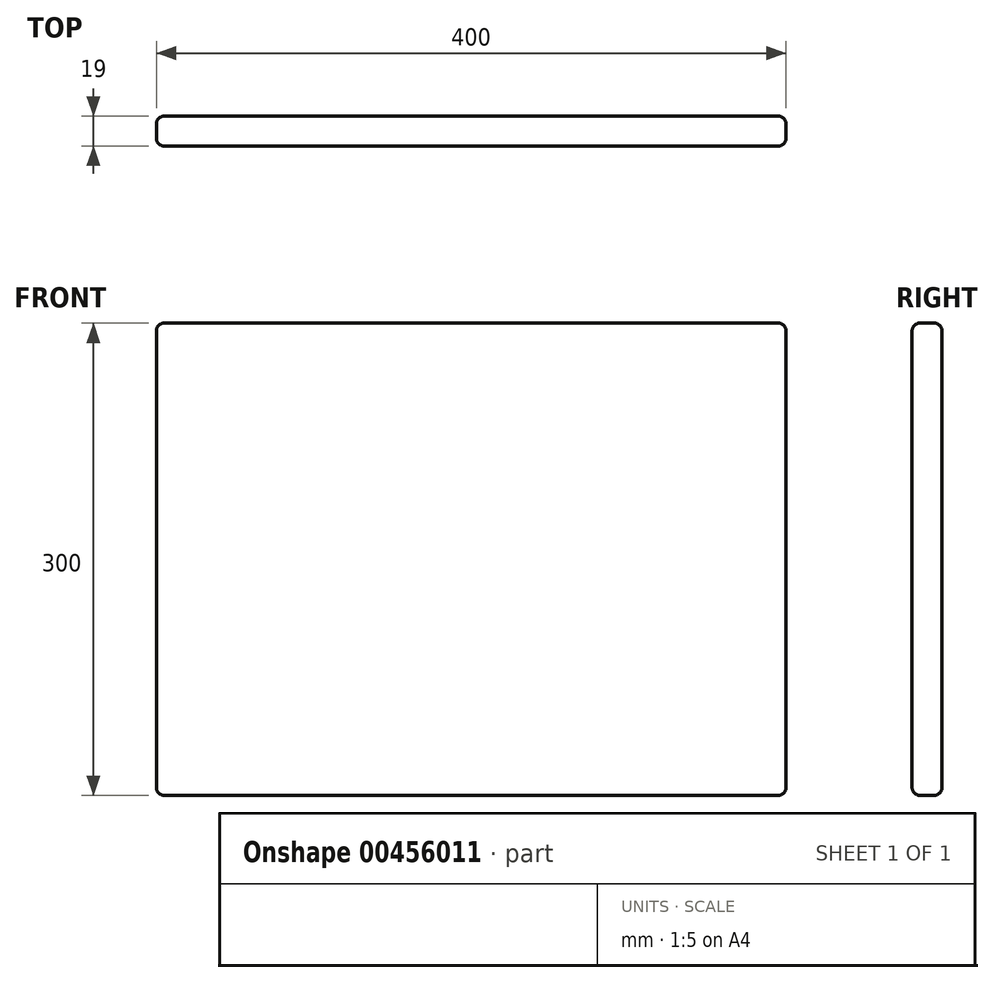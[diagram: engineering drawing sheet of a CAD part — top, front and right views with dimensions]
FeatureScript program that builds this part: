
annotation { "Feature Type Name" : "Feature", "Feature Type Description" : "" }
export const myFeature = defineFeature(function(context is Context, id is Id, definition is map)
    precondition{}
    {
        {
            var Q0;
            Q0=qCreatedBy(makeId("Front.planeOp"),FACE);
            var sketch = newSketch(context, id + "F0", { "sketchPlane" : qUnion([Q0])});
            skLineSegment(sketch, "E0", {"start": v(0, 0) * mm, "end": v(400, 0) * mm});
            skLineSegment(sketch, "E1", {"start": v(400, 0) * mm, "end": v(400, 300) * mm});
            skLineSegment(sketch, "E2", {"start": v(400, 300) * mm, "end": v(0, 300) * mm});
            skLineSegment(sketch, "E3", {"start": v(0, 300) * mm, "end": v(0, 0) * mm});
            skSolve(sketch);
        }
        {
            var Q0;
            Q0=makeQuery(id+"F0.imprint","IMPRINT",FACE,{"disambiguationData":[TD([[makeQuery(id+"F0.imprint","IMPRINT",EDGE,{"derivedFrom":sQuery(id+"F0.wireOp",EDGE,"E0")}),1.0]])]});
            extrude(context, id + "F1", {"entities" : qUnion([Q0]), "depth" : 19 * mm});
        }
        {
            var Q0;
            Q0=makeQuery(id+"F1.opExtrude","CAP_FACE",FACE,{"disambiguationData":[OSD([sQuery(id+"F0.wireOp",EDGE,"E0"),sQuery(id+"F0.wireOp",EDGE,"E1"),sQuery(id+"F0.wireOp",EDGE,"E2"),sQuery(id+"F0.wireOp",EDGE,"E3")])],"isStart":false});
            var Q1;
            Q1=makeQuery(id+"F1.opExtrude","SWEPT_FACE",FACE,{"disambiguationData":[OSD([sQuery(id+"F0.wireOp",EDGE,"E0")])]});
            var Q2;
            Q2=makeQuery(id+"F1.opExtrude","SWEPT_EDGE",EDGE,{"disambiguationData":[OSD([sQuery(id+"F0.wireOp",EDGE,"E0"),sQuery(id+"F0.wireOp",EDGE,"E1")])]});
            var Q3;
            Q3=makeQuery(id+"F1.opExtrude","SWEPT_EDGE",EDGE,{"disambiguationData":[OSD([sQuery(id+"F0.wireOp",EDGE,"E2"),sQuery(id+"F0.wireOp",EDGE,"E3")])]});
            var Q4;
            Q4=makeQuery(id+"F1.opExtrude","SWEPT_FACE",FACE,{"disambiguationData":[OSD([sQuery(id+"F0.wireOp",EDGE,"E1")])]});
            var Q5;
            Q5=makeQuery(id+"F1.opExtrude","SWEPT_FACE",FACE,{"disambiguationData":[OSD([sQuery(id+"F0.wireOp",EDGE,"E2")])]});
            var Q6;
            Q6=makeQuery(id+"F1.opExtrude","SWEPT_FACE",FACE,{"disambiguationData":[OSD([sQuery(id+"F0.wireOp",EDGE,"E3")])]});
            var Q7;
            Q7=makeQuery(id+"F1.opExtrude","CAP_EDGE",EDGE,{"disambiguationData":[OSD([sQuery(id+"F0.wireOp",EDGE,"E1")])],"isStart":false});
            var Q8;
            Q8=makeQuery(id+"F1.opExtrude","CAP_EDGE",EDGE,{"disambiguationData":[OSD([sQuery(id+"F0.wireOp",EDGE,"E2")])],"isStart":false});
            var Q9;
            Q9=makeQuery(id+"F1.opExtrude","CAP_EDGE",EDGE,{"disambiguationData":[OSD([sQuery(id+"F0.wireOp",EDGE,"E3")])],"isStart":true});
            var Q10;
            Q10=makeQuery(id+"F1.opExtrude","CAP_EDGE",EDGE,{"disambiguationData":[OSD([sQuery(id+"F0.wireOp",EDGE,"E3")])],"isStart":false});
            var Q11;
            Q11=makeQuery(id+"F1.opExtrude","CAP_FACE",FACE,{"disambiguationData":[OSD([sQuery(id+"F0.wireOp",EDGE,"E0"),sQuery(id+"F0.wireOp",EDGE,"E1"),sQuery(id+"F0.wireOp",EDGE,"E2"),sQuery(id+"F0.wireOp",EDGE,"E3")])],"isStart":true});
            var Q12;
            Q12=makeQuery(id+"F1.opExtrude","SWEPT_EDGE",EDGE,{"disambiguationData":[OSD([sQuery(id+"F0.wireOp",EDGE,"E1"),sQuery(id+"F0.wireOp",EDGE,"E2")])]});
            var Q13;
            Q13=makeQuery(id+"F1.opExtrude","SWEPT_EDGE",EDGE,{"disambiguationData":[OSD([sQuery(id+"F0.wireOp",EDGE,"E0"),sQuery(id+"F0.wireOp",EDGE,"E3")])]});
            var Q14;
            Q14=makeQuery(id+"F1.opExtrude","CAP_EDGE",EDGE,{"disambiguationData":[OSD([sQuery(id+"F0.wireOp",EDGE,"E1")])],"isStart":true});
            var Q15;
            Q15=makeQuery(id+"F1.opExtrude","CAP_EDGE",EDGE,{"disambiguationData":[OSD([sQuery(id+"F0.wireOp",EDGE,"E2")])],"isStart":true});
            fillet(context, id + "F2", {"entities" : qUnion([Q0, Q1, Q2, Q3, Q4, Q5, Q6, Q7, Q8, Q9, Q10, Q11, Q12, Q13, Q14, Q15]), "radius" : 5 * mm, "tangentPropagation" : true, "allowEdgeOverflow" : false});
        }
    });
